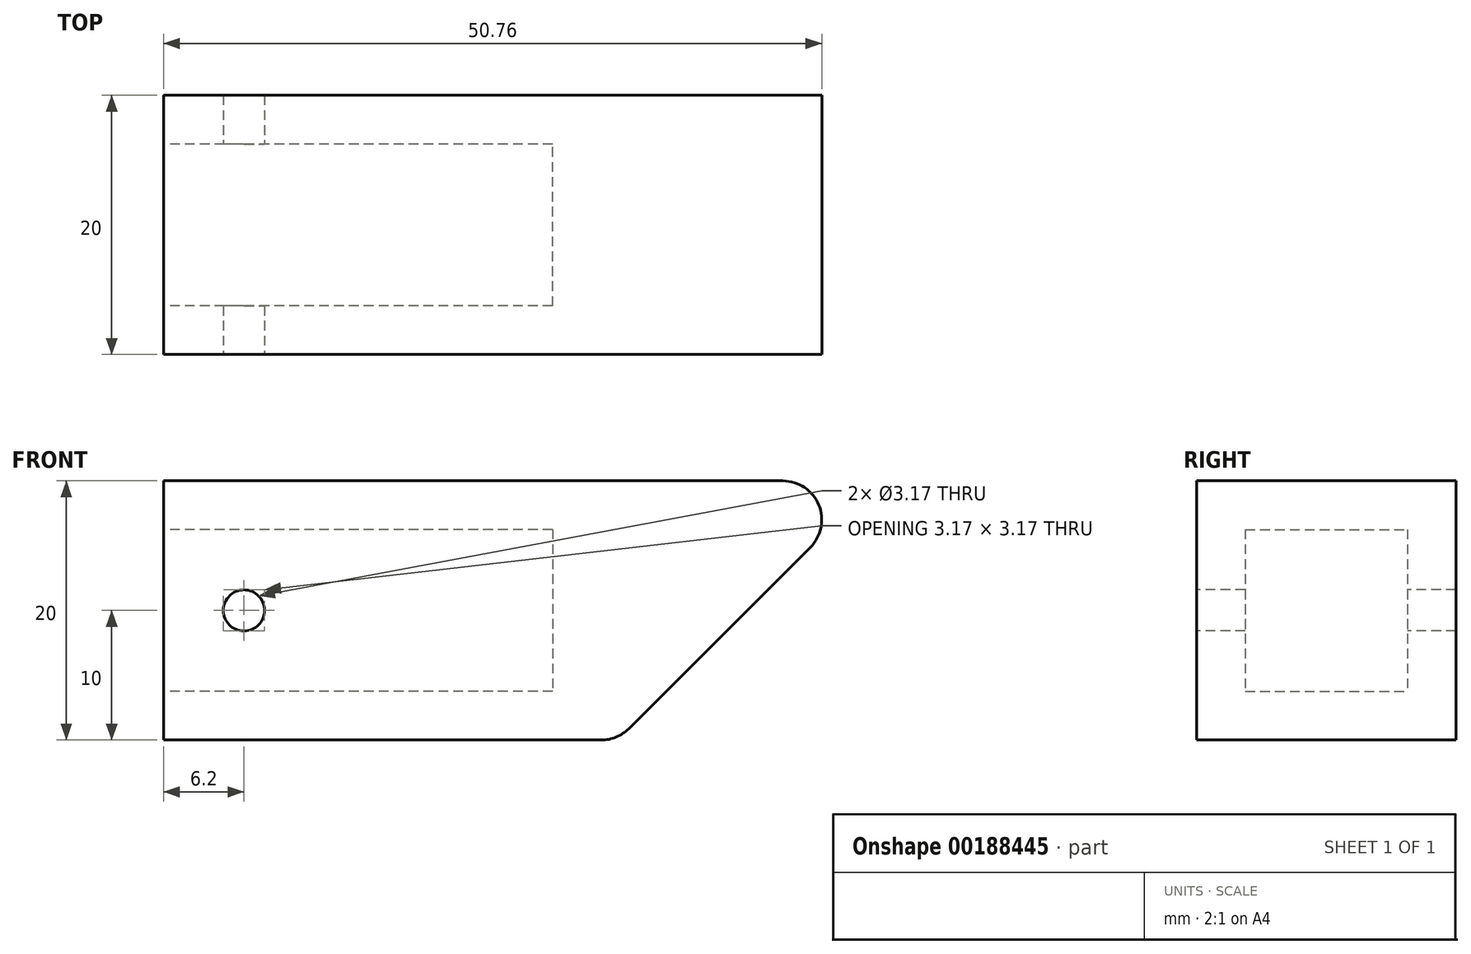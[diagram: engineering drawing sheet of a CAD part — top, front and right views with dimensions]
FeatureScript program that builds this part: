
annotation { "Feature Type Name" : "Feature", "Feature Type Description" : "" }
export const myFeature = defineFeature(function(context is Context, id is Id, definition is map)
    precondition{}
    {
        {
            var Q0;
            Q0=qCreatedBy(makeId("Front.planeOp"),FACE);
            var sketch = newSketch(context, id + "F0", { "sketchPlane" : qUnion([Q0])});
            skLineSegment(sketch, "E0.bottom", {"start": v(0, 10) * mm, "end": v(47.76, 10) * mm});
            skLineSegment(sketch, "E0.top", {"start": v(0, -10) * mm, "end": v(33.76, -10) * mm});
            skLineSegment(sketch, "E0.left", {"start": v(0, 10) * mm, "end": v(0, -10) * mm});
            skLineSegment(sketch, "E1", {"start": v(49.88, 4.88) * mm, "end": v(35.88, -9.12) * mm});
            skPoint(sketch, "E2.visualSharp", {"position": v(55, 10) * mm});
            skArc(sketch, "E2.filletArc", {"start": v(49.88, 4.88) * mm, "mid": v(50.53, 8.15) * mm, "end": v(47.76, 10) * mm});
            skPoint(sketch, "E3.visualSharp", {"position": v(35, -10) * mm});
            skArc(sketch, "E3.filletArc", {"start": v(33.76, -10) * mm, "mid": v(34.9, -9.77) * mm, "end": v(35.88, -9.12) * mm});
            skPoint(sketch, "E4", {"position": v(0, 0) * mm});
            skSolve(sketch);
        }
        {
            var Q0;
            Q0 = qSketchRegion(id + "F0", true);
            extrude(context, id + "F1", {"entities" : qUnion([Q0]), "endBound" : BoundingType.SYMMETRIC, "depth" : 20 * mm, "offsetDistance" : 25 * mm});
        }
        {
            var Q0;
            Q0=makeQuery(id+"F1.opExtrude","SWEPT_FACE",FACE,{"disambiguationData":[OSD([sQuery(id+"F0.wireOp",EDGE,"E0.left")])]});
            var sketch = newSketch(context, id + "F2", { "sketchPlane" : qUnion([Q0])});
            skLineSegment(sketch, "E5.bottom", {"start": v(6.25, 6.25) * mm, "end": v(-6.25, 6.25) * mm});
            skLineSegment(sketch, "E5.top", {"start": v(6.25, -6.25) * mm, "end": v(-6.25, -6.25) * mm});
            skLineSegment(sketch, "E5.left", {"start": v(6.25, 6.25) * mm, "end": v(6.25, -6.25) * mm});
            skLineSegment(sketch, "E5.right", {"start": v(-6.25, 6.25) * mm, "end": v(-6.25, -6.25) * mm});
            skPoint(sketch, "E5.middle", {"position": v(0, 0) * mm});
            skSolve(sketch);
        }
        {
            var Q0;
            Q0 = qSketchRegion(id + "F2", true);
            extrude(context, id + "F3", {"entities" : qUnion([Q0]), "operationType" : NewBodyOperationType.REMOVE, "oppositeDirection" : true, "depth" : 30 * mm, "offsetDistance" : 25 * mm});
        }
        {
            var Q0;
            Q0=makeQuery(id+"F1.opExtrude","CAP_FACE",FACE,{"disambiguationData":[OSD([sQuery(id+"F0.wireOp",EDGE,"E0.bottom"),sQuery(id+"F0.wireOp",EDGE,"E0.top"),sQuery(id+"F0.wireOp",EDGE,"E0.left"),sQuery(id+"F0.wireOp",EDGE,"E1"),sQuery(id+"F0.wireOp",EDGE,"E2.filletArc"),sQuery(id+"F0.wireOp",EDGE,"E3.filletArc")])],"isStart":false});
            var sketch = newSketch(context, id + "F4", { "sketchPlane" : qUnion([Q0])});
            skPoint(sketch, "E6", {"position": v(6.2, 0) * mm});
            skSolve(sketch);
        }
        {
            var Q0;
            Q0=sQuery(id+"F4.wireOp",VERTEX,"E6");
            var Q1;
            Q1=makeQuery(id+"F1.opExtrude","SWEPT_BODY",BODY,{"disambiguationData":[OSD([sQuery(id+"F0.wireOp",EDGE,"E0.bottom"),sQuery(id+"F0.wireOp",EDGE,"E0.top"),sQuery(id+"F0.wireOp",EDGE,"E0.left"),sQuery(id+"F0.wireOp",EDGE,"E1"),sQuery(id+"F0.wireOp",EDGE,"E2.filletArc"),sQuery(id+"F0.wireOp",EDGE,"E3.filletArc")])]});
            hole(context, id + "F5", {"style" : HoleStyle.SIMPLE, "endStyle" : HoleEndStyle.THROUGH, "holeDiameter" : 3.17 * mm, "majorDiameter" : 5 * mm, "isTappedThrough" : true, "tappedDepth" : 12 * mm, "tapClearance" : 3, "startFromSketch" : true, "locations" : qUnion([Q0]), "scope" : qUnion([Q1])});
        }
    });
